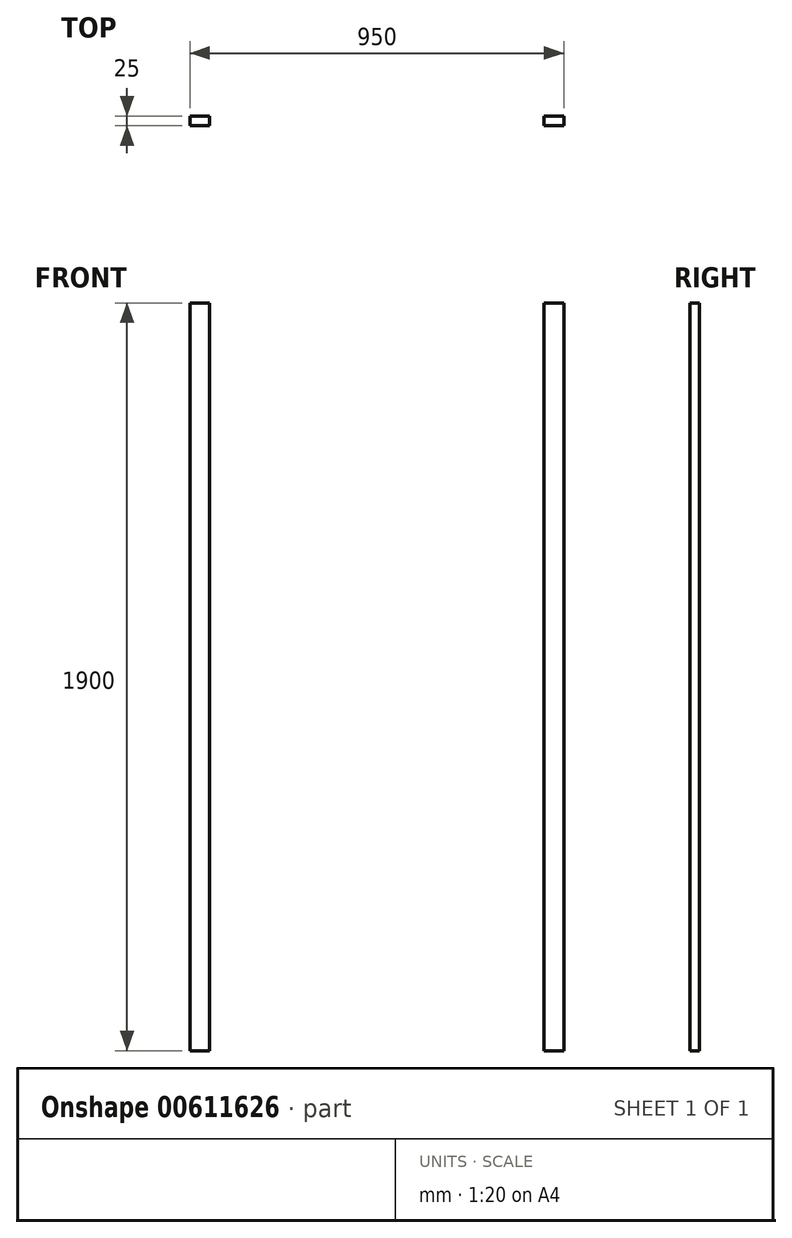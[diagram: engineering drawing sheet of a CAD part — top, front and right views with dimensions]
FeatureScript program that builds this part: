
annotation { "Feature Type Name" : "Feature", "Feature Type Description" : "" }
export const myFeature = defineFeature(function(context is Context, id is Id, definition is map)
    precondition{}
    {
        {
            var Q0;
            Q0=qCreatedBy(makeId("Front.planeOp"),FACE);
            var sketch = newSketch(context, id + "F0", { "sketchPlane" : qUnion([Q0])});
            skLineSegment(sketch, "E0.left", {"start": v(0, 0) * mm, "end": v(0, 1900) * mm});
            skLineSegment(sketch, "E0.right", {"start": v(-850, 0) * mm, "end": v(-850, 1900) * mm});
            skLineSegment(sketch, "E1.left", {"start": v(50, 1900) * mm, "end": v(50, 0) * mm});
            skLineSegment(sketch, "E1.right", {"start": v(-900, 1900) * mm, "end": v(-900, 0) * mm});
            skLineSegment(sketch, "E2", {"start": v(50, 1900) * mm, "end": v(0, 1900) * mm});
            skLineSegment(sketch, "E3", {"start": v(-850, 1900) * mm, "end": v(-900, 1900) * mm});
            skLineSegment(sketch, "E4", {"start": v(-850, 0) * mm, "end": v(-900, 0) * mm});
            skLineSegment(sketch, "E5", {"start": v(50, 0) * mm, "end": v(0, 0) * mm});
            skSolve(sketch);
        }
        {
            var Q0;
            Q0=makeQuery(id+"F0.imprint","IMPRINT",FACE,{"disambiguationData":[TD([[makeQuery(id+"F0.imprint","IMPRINT",EDGE,{"derivedFrom":sQuery(id+"F0.wireOp",EDGE,"E0.left")}),-1.0]])]});
            var Q1;
            Q1=makeQuery(id+"F0.imprint","IMPRINT",FACE,{"disambiguationData":[TD([[makeQuery(id+"F0.imprint","IMPRINT",EDGE,{"derivedFrom":sQuery(id+"F0.wireOp",EDGE,"E0.right")}),1.0]])]});
            extrude(context, id + "F1", {"entities" : qUnion([Q0, Q1]), "depth" : 25 * mm, "offsetDistance" : 25 * mm});
        }
    });
